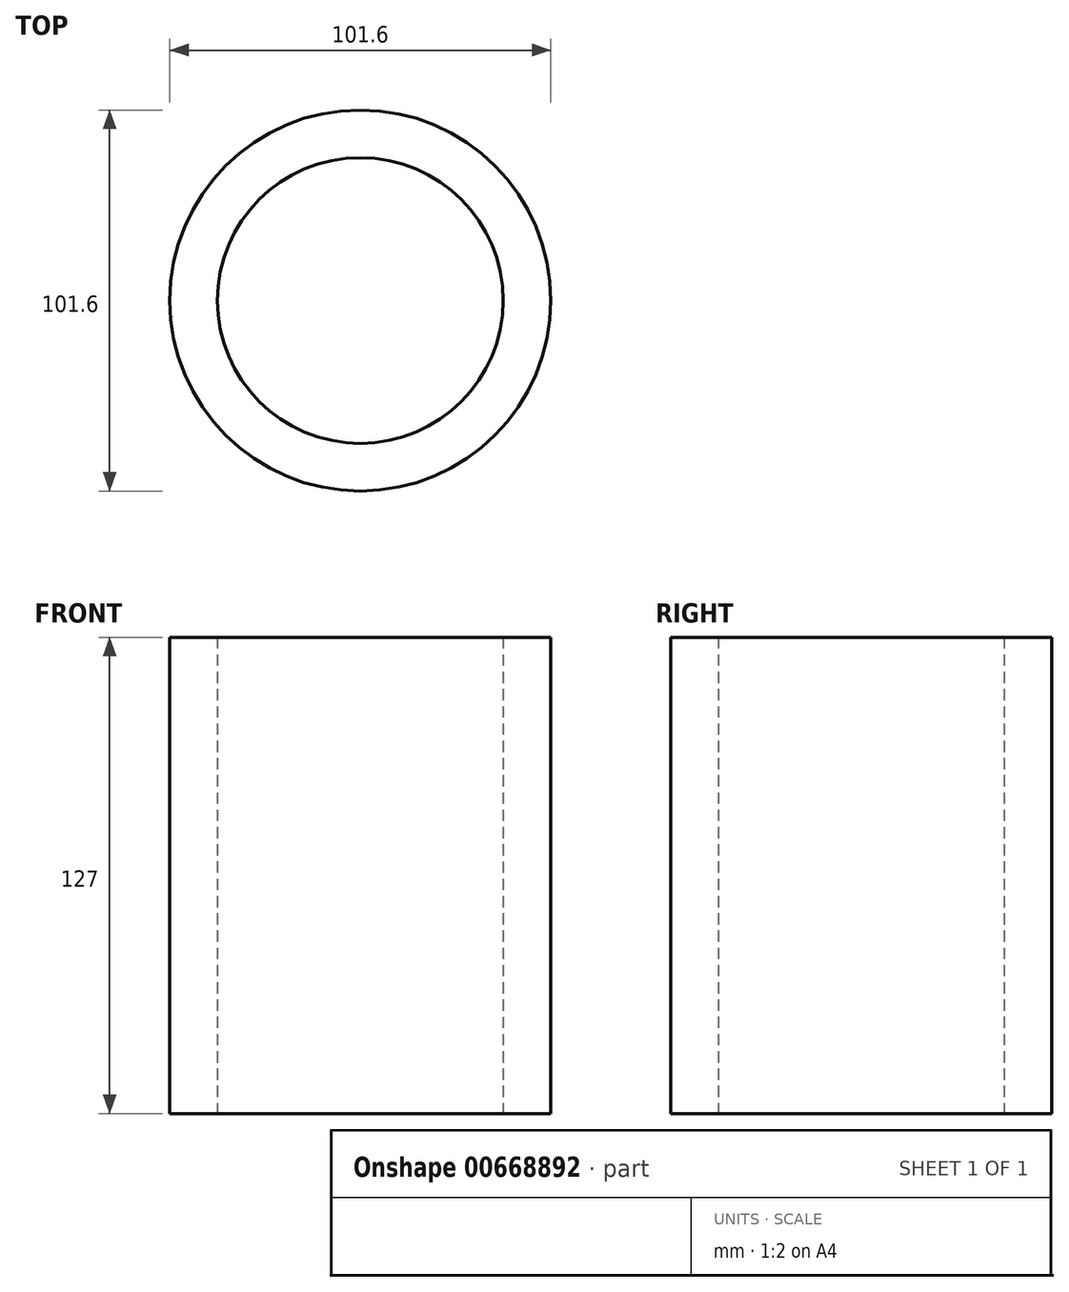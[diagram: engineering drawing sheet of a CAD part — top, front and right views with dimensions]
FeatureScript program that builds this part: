
annotation { "Feature Type Name" : "Feature", "Feature Type Description" : "" }
export const myFeature = defineFeature(function(context is Context, id is Id, definition is map)
    precondition{}
    {
        {
            var Q0;
            Q0=qCreatedBy(makeId("Top.planeOp"),FACE);
            var sketch = newSketch(context, id + "F0", { "sketchPlane" : qUnion([Q0])});
            skCircle(sketch, "E0", {"center": v(0, 0) * mm, "radius": 50.8 * mm});
            skCircle(sketch, "E1", {"center": v(0, 0) * mm, "radius": 38.1 * mm});
            skSolve(sketch);
        }
        {
            var Q0;
            Q0 = qSketchRegion(id + "F0", true);
            extrude(context, id + "F1", {"entities" : qUnion([Q0]), "depth" : 127 * mm, "offsetDistance" : 25.4 * mm});
        }
    });
